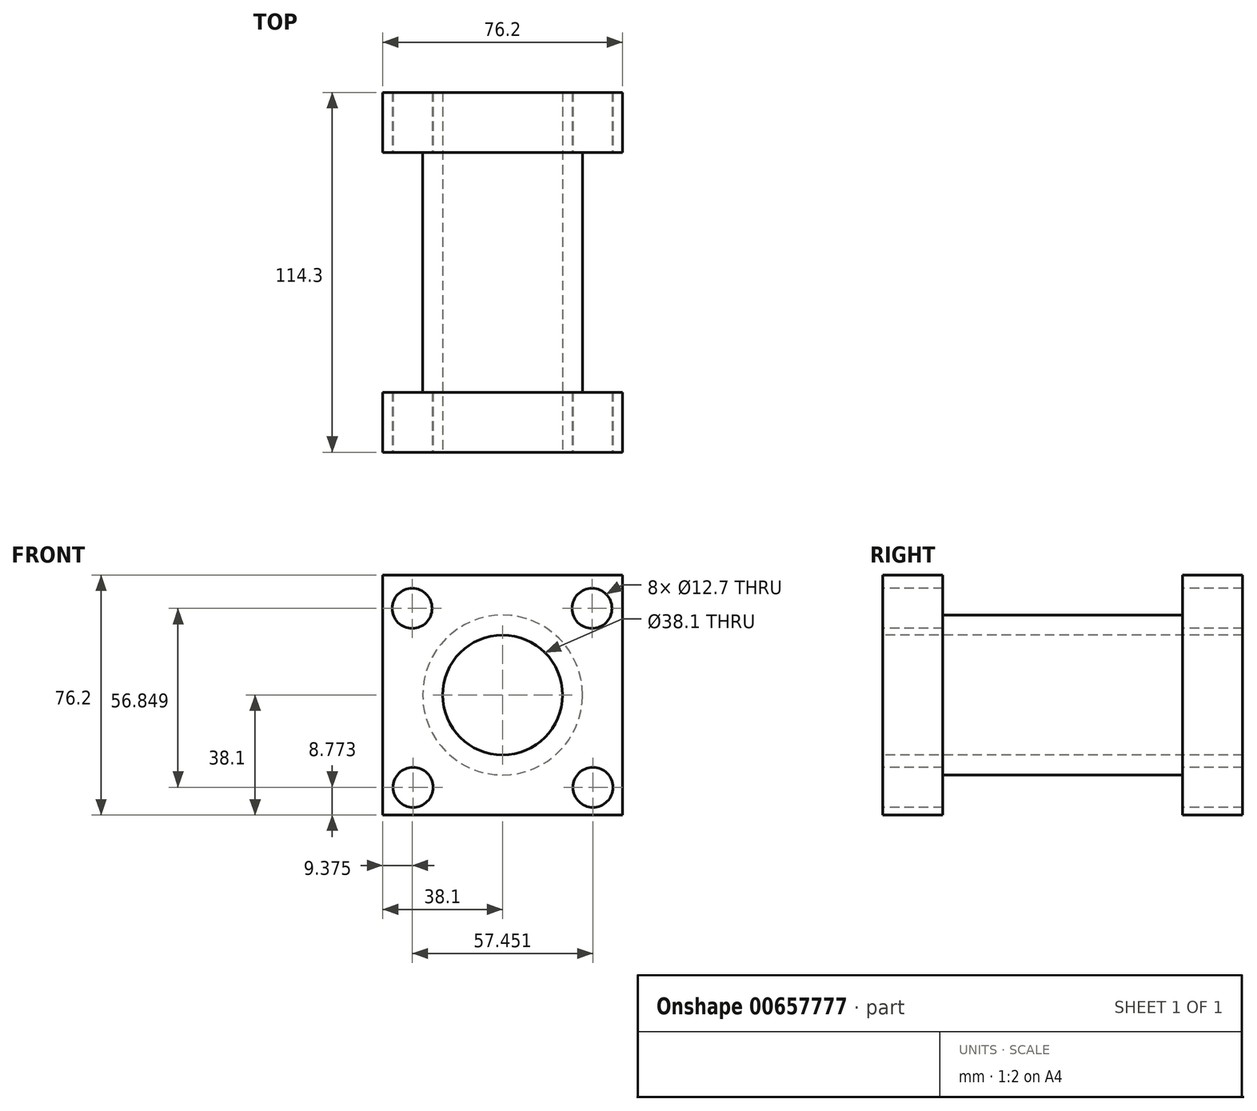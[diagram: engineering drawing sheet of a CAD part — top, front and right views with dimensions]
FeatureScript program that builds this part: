
annotation { "Feature Type Name" : "Feature", "Feature Type Description" : "" }
export const myFeature = defineFeature(function(context is Context, id is Id, definition is map)
    precondition{}
    {
        {
            var Q0;
            Q0=qCreatedBy(makeId("Front.planeOp"),FACE);
            var sketch = newSketch(context, id + "F0", { "sketchPlane" : qUnion([Q0])});
            skLineSegment(sketch, "E0.bottom", {"start": v(38.1, -38.1) * mm, "end": v(-38.1, -38.1) * mm});
            skLineSegment(sketch, "E0.top", {"start": v(38.1, 38.1) * mm, "end": v(-38.1, 38.1) * mm});
            skLineSegment(sketch, "E0.left", {"start": v(38.1, -38.1) * mm, "end": v(38.1, 38.1) * mm});
            skLineSegment(sketch, "E0.right", {"start": v(-38.1, -38.1) * mm, "end": v(-38.1, 38.1) * mm});
            skPoint(sketch, "E0.middle", {"position": v(0, 0) * mm});
            skSolve(sketch);
        }
        {
            var Q0;
            Q0 = qSketchRegion(id + "F0", true);
            extrude(context, id + "F1", {"entities" : qUnion([Q0]), "depth" : 19.05 * mm, "offsetDistance" : 25.4 * mm});
        }
        {
            var Q0;
            Q0=makeQuery(id+"F1.opExtrude","CAP_FACE",FACE,{"disambiguationData":[OSD([sQuery(id+"F0.wireOp",EDGE,"E0.bottom"),sQuery(id+"F0.wireOp",EDGE,"E0.top"),sQuery(id+"F0.wireOp",EDGE,"E0.left"),sQuery(id+"F0.wireOp",EDGE,"E0.right")])],"isStart":false});
            var sketch = newSketch(context, id + "F2", { "sketchPlane" : qUnion([Q0])});
            skCircle(sketch, "E1", {"center": v(0, 0) * mm, "radius": 25.4 * mm});
            skSolve(sketch);
        }
        {
            var Q0;
            Q0 = qSketchRegion(id + "F2", true);
            extrude(context, id + "F3", {"entities" : qUnion([Q0]), "operationType" : NewBodyOperationType.ADD, "depth" : 76.2 * mm, "offsetDistance" : 25.4 * mm});
        }
        {
            var Q0;
            Q0=makeQuery(id+"F3.opExtrude","CAP_FACE",FACE,{"disambiguationData":[OSD([sQuery(id+"F2.wireOp",EDGE,"E1")])],"isStart":false});
            var sketch = newSketch(context, id + "F4", { "sketchPlane" : qUnion([Q0])});
            skLineSegment(sketch, "E2.bottom", {"start": v(38.1, -38.1) * mm, "end": v(-38.1, -38.1) * mm});
            skLineSegment(sketch, "E2.top", {"start": v(38.1, 38.1) * mm, "end": v(-38.1, 38.1) * mm});
            skLineSegment(sketch, "E2.left", {"start": v(38.1, -38.1) * mm, "end": v(38.1, 38.1) * mm});
            skLineSegment(sketch, "E2.right", {"start": v(-38.1, -38.1) * mm, "end": v(-38.1, 38.1) * mm});
            skPoint(sketch, "E2.middle", {"position": v(0, 0) * mm});
            skSolve(sketch);
        }
        {
            var Q0;
            Q0 = qSketchRegion(id + "F4", true);
            extrude(context, id + "F5", {"entities" : qUnion([Q0]), "operationType" : NewBodyOperationType.ADD, "depth" : 19.05 * mm, "offsetDistance" : 25.4 * mm});
        }
        {
            var Q0;
            Q0=makeQuery(id+"F5.opExtrude","CAP_FACE",FACE,{"disambiguationData":[OSD([sQuery(id+"F4.wireOp",EDGE,"E2.bottom"),sQuery(id+"F4.wireOp",EDGE,"E2.top"),sQuery(id+"F4.wireOp",EDGE,"E2.left"),sQuery(id+"F4.wireOp",EDGE,"E2.right")])],"isStart":false});
            var sketch = newSketch(context, id + "F6", { "sketchPlane" : qUnion([Q0])});
            skCircle(sketch, "E3", {"center": v(0, 0) * mm, "radius": 19.05 * mm});
            skSolve(sketch);
        }
        {
            var Q0;
            Q0=makeQuery(id+"F6.imprint","IMPRINT",FACE,{"disambiguationData":[TD([[makeQuery(id+"F6.imprint","IMPRINT",EDGE,{"derivedFrom":sQuery(id+"F6.wireOp",EDGE,"E3")}),-1.0]])]});
            var sketch = newSketch(context, id + "F7", { "sketchPlane" : qUnion([Q0])});
            skLineSegment(sketch, "E4", {"start": v(-38.35, 36.95) * mm, "end": v(-38.35, 27.42) * mm});
            skLineSegment(sketch, "E5", {"start": v(-38.35, 27.42) * mm, "end": v(-28.83, 27.42) * mm});
            skLineSegment(sketch, "E6", {"start": v(-28.83, 27.42) * mm, "end": v(-28.83, -29.73) * mm});
            skLineSegment(sketch, "E7", {"start": v(-28.83, -29.73) * mm, "end": v(28.32, -29.73) * mm});
            skLineSegment(sketch, "E8", {"start": v(28.32, -29.73) * mm, "end": v(28.32, 27.42) * mm});
            skLineSegment(sketch, "E9", {"start": v(-28.83, 27.42) * mm, "end": v(28.32, 27.42) * mm});
            skSolve(sketch);
        }
        {
            var Q0;
            Q0 = qSketchRegion(id + "F6", true);
            extrude(context, id + "F8", {"entities" : qUnion([Q0]), "operationType" : NewBodyOperationType.REMOVE, "oppositeDirection" : true, "depth" : 114.3 * mm, "offsetDistance" : 25.4 * mm});
        }
        {
            var Q0;
            Q0=makeQuery(id+"F7.imprint","IMPRINT",FACE,{"disambiguationData":[TD([[makeQuery(id+"F7.imprint","IMPRINT",EDGE,{"derivedFrom":sQuery(id+"F7.wireOp",EDGE,"E6")}),-1.0]])]});
            var sketch = newSketch(context, id + "F9", { "sketchPlane" : qUnion([Q0])});
            skCircle(sketch, "E10", {"center": v(-28.73, 27.52) * mm, "radius": 6.35 * mm});
            skCircle(sketch, "E11", {"center": v(-28.42, -29.33) * mm, "radius": 6.35 * mm});
            skCircle(sketch, "E12", {"center": v(28.73, -29.33) * mm, "radius": 6.35 * mm});
            skCircle(sketch, "E13", {"center": v(28.42, 27.52) * mm, "radius": 6.35 * mm});
            skSolve(sketch);
        }
        {
            var Q0;
            Q0 = qSketchRegion(id + "F9", true);
            extrude(context, id + "F10", {"entities" : qUnion([Q0]), "operationType" : NewBodyOperationType.REMOVE, "oppositeDirection" : true, "depth" : 114.3 * mm, "offsetDistance" : 25.4 * mm});
        }
    });
